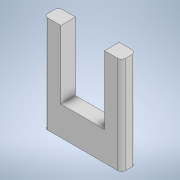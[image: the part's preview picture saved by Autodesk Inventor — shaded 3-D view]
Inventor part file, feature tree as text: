
AUTODESK INVENTOR PART (.ipt)
format: ipt  version: 2021 (Build 250183000, 183)  size: 259,584 bytes
history: native  units: in
note: dims shown in document units (in); Inventor stores cm internally (conversion verified against a paired STEP export)
features: extrude x2, sketch x2, fillet x1, projected_geometry x1
ambient origin geometry x8: Origin, YZ Plane, XZ Plane, XY Plane, X Axis, Y Axis, Z Axis, Center Point
bodies: Solid1 (feature_tree)
feature tree (6):
  extrude  "Extrusion1"  Depth=0.3937in
  extrude  "Extrusion2"  Depth=0.1772in
  fillet  "Fillet1"  Radius=0.2756in
  sketch  "Sketch1"  dims[d0=0.315in d1=0.3937in]
  sketch  "Sketch2"  dims[d2=0.0591in d3=0.0in d4=0.1772in d5=0.2756in d6=0.0in d7=0.0in d8=0.0157in]
  projected_geometry  "Projected Loop1"
